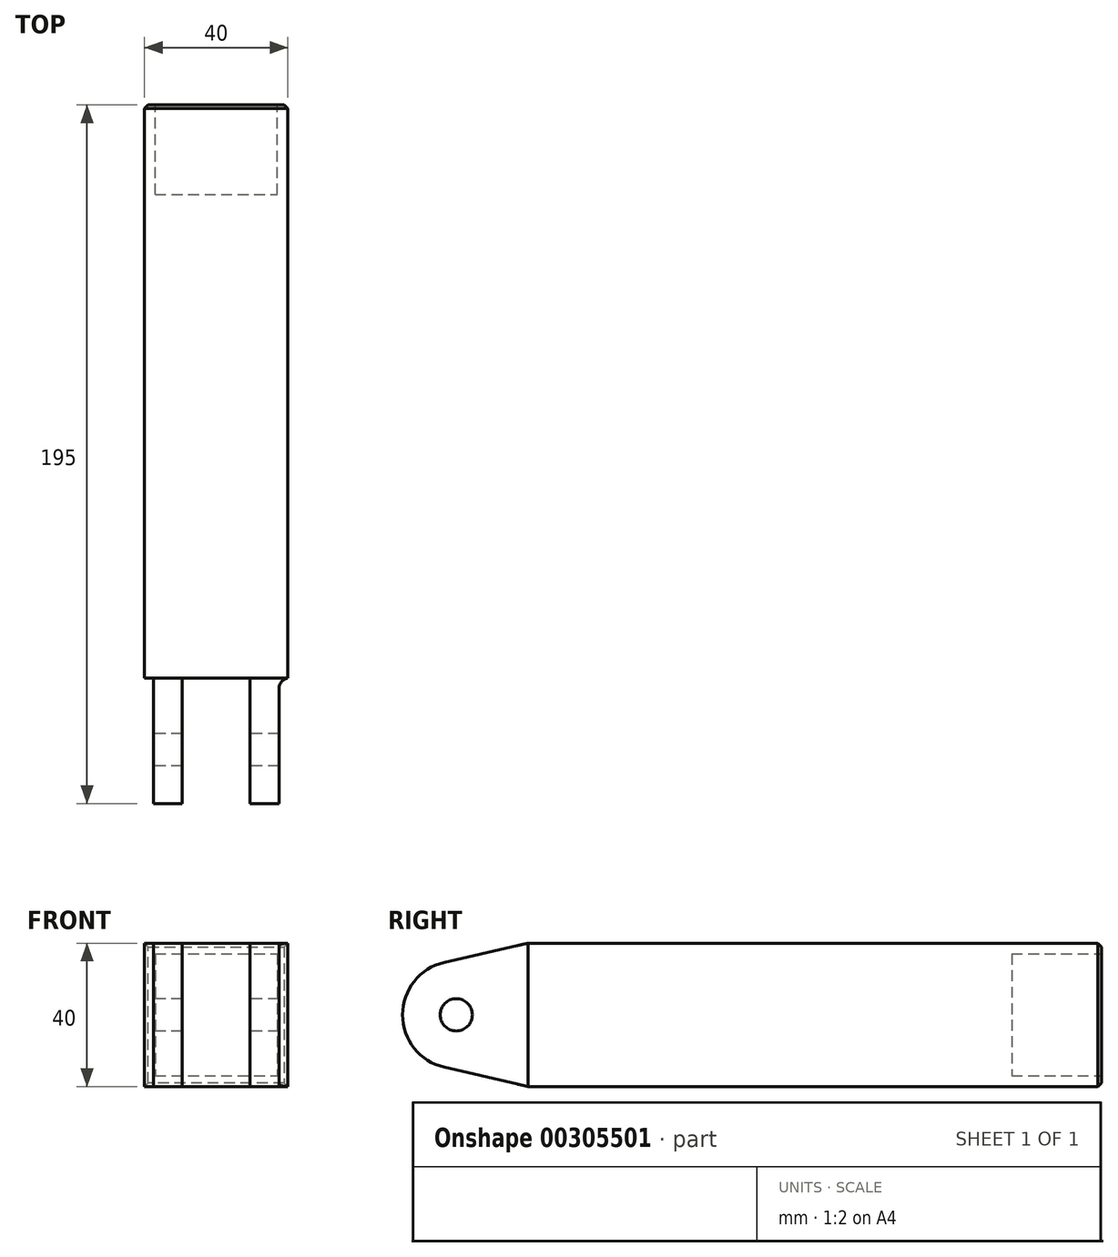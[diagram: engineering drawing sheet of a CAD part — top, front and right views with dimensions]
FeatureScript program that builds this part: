
annotation { "Feature Type Name" : "Feature", "Feature Type Description" : "" }
export const myFeature = defineFeature(function(context is Context, id is Id, definition is map)
    precondition{}
    {
        {
            var Q0;
            Q0=qCreatedBy(makeId("Right.planeOp"),FACE);
            var sketch = newSketch(context, id + "F0", { "sketchPlane" : qUnion([Q0])});
            skLineSegment(sketch, "E0.bottom", {"start": v(80, 20) * mm, "end": v(-80, 20) * mm});
            skLineSegment(sketch, "E0.top", {"start": v(80, -20) * mm, "end": v(-80, -20) * mm});
            skLineSegment(sketch, "E0.left", {"start": v(80, 20) * mm, "end": v(80, -20) * mm});
            skLineSegment(sketch, "E0.right", {"start": v(-80, 20) * mm, "end": v(-80, -20) * mm});
            skPoint(sketch, "E0.middle", {"position": v(0, 0) * mm});
            skSolve(sketch);
        }
        {
            var Q0;
            Q0=makeQuery(id+"F0.imprint","IMPRINT",FACE,{"disambiguationData":[TD([[makeQuery(id+"F0.imprint","IMPRINT",EDGE,{"derivedFrom":sQuery(id+"F0.wireOp",EDGE,"E0.bottom")}),1.0]])]});
            extrude(context, id + "F1", {"entities" : qUnion([Q0]), "endBound" : BoundingType.SYMMETRIC, "depth" : 40 * mm});
        }
        {
            var Q0;
            Q0=makeQuery(id+"F1.opExtrude","SWEPT_FACE",FACE,{"disambiguationData":[OSD([sQuery(id+"F0.wireOp",EDGE,"E0.left")])]});
            var sketch = newSketch(context, id + "F2", { "sketchPlane" : qUnion([Q0])});
            skLineSegment(sketch, "E1.bottom", {"start": v(17, 17) * mm, "end": v(-17, 17) * mm});
            skLineSegment(sketch, "E1.top", {"start": v(17, -17) * mm, "end": v(-17, -17) * mm});
            skLineSegment(sketch, "E1.left", {"start": v(17, 17) * mm, "end": v(17, -17) * mm});
            skLineSegment(sketch, "E1.right", {"start": v(-17, 17) * mm, "end": v(-17, -17) * mm});
            skPoint(sketch, "E1.middle", {"position": v(0, 0) * mm});
            skSolve(sketch);
        }
        {
            var Q0;
            Q0=makeQuery(id+"F2.imprint","IMPRINT",FACE,{"disambiguationData":[TD([[makeQuery(id+"F2.imprint","IMPRINT",EDGE,{"derivedFrom":sQuery(id+"F2.wireOp",EDGE,"E1.bottom")}),1.0]])]});
            extrude(context, id + "F3", {"entities" : qUnion([Q0]), "operationType" : NewBodyOperationType.REMOVE, "oppositeDirection" : true, "depth" : 25 * mm});
        }
        {
            var Q0;
            Q0=qCreatedBy(makeId("Right.planeOp"),FACE);
            var sketch = newSketch(context, id + "F4", { "sketchPlane" : qUnion([Q0])});
            skLineSegment(sketch, "E2", {"start": v(0, 0) * mm, "end": v(-100, 0) * mm, "construction": true});
            skCircle(sketch, "E3", {"center": v(-100, 0) * mm, "radius": 4.5 * mm});
            skArc(sketch, "E4", {"start": v(-103.37, 14.62) * mm, "mid": v(-115, 0) * mm, "end": v(-103.37, -14.62) * mm});
            skLineSegment(sketch, "E5", {"start": v(-100, 0) * mm, "end": v(-80, 0) * mm, "construction": true});
            skLineSegment(sketch, "E6", {"start": v(-80, 0) * mm, "end": v(-80, 20) * mm});
            skLineSegment(sketch, "E7", {"start": v(-80, 20) * mm, "end": v(-103.37, 14.62) * mm});
            skLineSegment(sketch, "E8", {"start": v(-80, 0) * mm, "end": v(-80, -20) * mm});
            skLineSegment(sketch, "E9", {"start": v(-80, -20) * mm, "end": v(-103.37, -14.62) * mm});
            skSolve(sketch);
        }
        {
            var Q0;
            Q0=makeQuery(id+"F4.imprint","IMPRINT",FACE,{"disambiguationData":[TD([[makeQuery(id+"F4.imprint","IMPRINT",EDGE,{"derivedFrom":sQuery(id+"F4.wireOp",EDGE,"E3")}),-1.0]])]});
            extrude(context, id + "F5", {"entities" : qUnion([Q0]), "operationType" : NewBodyOperationType.ADD, "endBound" : BoundingType.SYMMETRIC, "depth" : 35 * mm});
        }
        {
            var Q0;
            Q0=qCreatedBy(makeId("Top.planeOp"),FACE);
            var sketch = newSketch(context, id + "F6", { "sketchPlane" : qUnion([Q0])});
            skLineSegment(sketch, "E10", {"start": v(0, 0) * mm, "end": v(0, -80) * mm, "construction": true});
            skLineSegment(sketch, "E11", {"start": v(0, -80) * mm, "end": v(0, -115) * mm, "construction": true});
            skLineSegment(sketch, "E12", {"start": v(0, -115) * mm, "end": v(9.5, -115) * mm});
            skLineSegment(sketch, "E13", {"start": v(9.5, -115) * mm, "end": v(9.5, -80) * mm});
            skLineSegment(sketch, "E14", {"start": v(9.5, -80) * mm, "end": v(-9.5, -80) * mm});
            skLineSegment(sketch, "E15", {"start": v(-9.5, -80) * mm, "end": v(-9.5, -115) * mm});
            skLineSegment(sketch, "E16", {"start": v(-9.5, -115) * mm, "end": v(0, -115) * mm});
            skSolve(sketch);
        }
        {
            var Q0;
            Q0=makeQuery(id+"F6.imprint","IMPRINT",FACE,{"disambiguationData":[TD([[makeQuery(id+"F6.imprint","IMPRINT",EDGE,{"derivedFrom":sQuery(id+"F6.wireOp",EDGE,"E12")}),1.0]])]});
            extrude(context, id + "F7", {"entities" : qUnion([Q0]), "operationType" : NewBodyOperationType.REMOVE, "endBound" : BoundingType.SYMMETRIC, "oppositeDirection" : true, "depth" : 50 * mm});
        }
        {
            var Q0;
            Q0=makeQuery(id+"F5.opExtrude","CAP_EDGE",EDGE,{"disambiguationData":[OSD([sQuery(id+"F4.wireOp",EDGE,"E6"),sQuery(id+"F4.wireOp",EDGE,"E8")])],"isStart":true});
            var Q1;
            Q1=makeQuery(id+"F5.opExtrude","CAP_EDGE",EDGE,{"disambiguationData":[OSD([sQuery(id+"F4.wireOp",EDGE,"E6"),sQuery(id+"F4.wireOp",EDGE,"E8")])],"isStart":false});
            fillet(context, id + "F8", {"entities" : qUnion([Q0, Q1]), "radius" : 3 * mm, "tangentPropagation" : true, "allowEdgeOverflow" : false});
        }
        {
            var Q0;
            Q0=makeQuery(id+"F1.opExtrude","SWEPT_EDGE",EDGE,{"disambiguationData":[OSD([sQuery(id+"F0.wireOp",EDGE,"E0.bottom"),sQuery(id+"F0.wireOp",EDGE,"E0.left")])]});
            var Q1;
            Q1=makeQuery(id+"F1.opExtrude","CAP_EDGE",EDGE,{"disambiguationData":[OSD([sQuery(id+"F0.wireOp",EDGE,"E0.left")])],"isStart":true});
            var Q2;
            Q2=makeQuery(id+"F1.opExtrude","SWEPT_EDGE",EDGE,{"disambiguationData":[OSD([sQuery(id+"F0.wireOp",EDGE,"E0.top"),sQuery(id+"F0.wireOp",EDGE,"E0.left")])]});
            var Q3;
            Q3=makeQuery(id+"F1.opExtrude","CAP_EDGE",EDGE,{"disambiguationData":[OSD([sQuery(id+"F0.wireOp",EDGE,"E0.left")])],"isStart":false});
            chamfer(context, id + "F9", {"entities" : qUnion([Q0, Q1, Q2, Q3]), "width" : 1 * mm, "tangentPropagation" : true});
        }
    });
